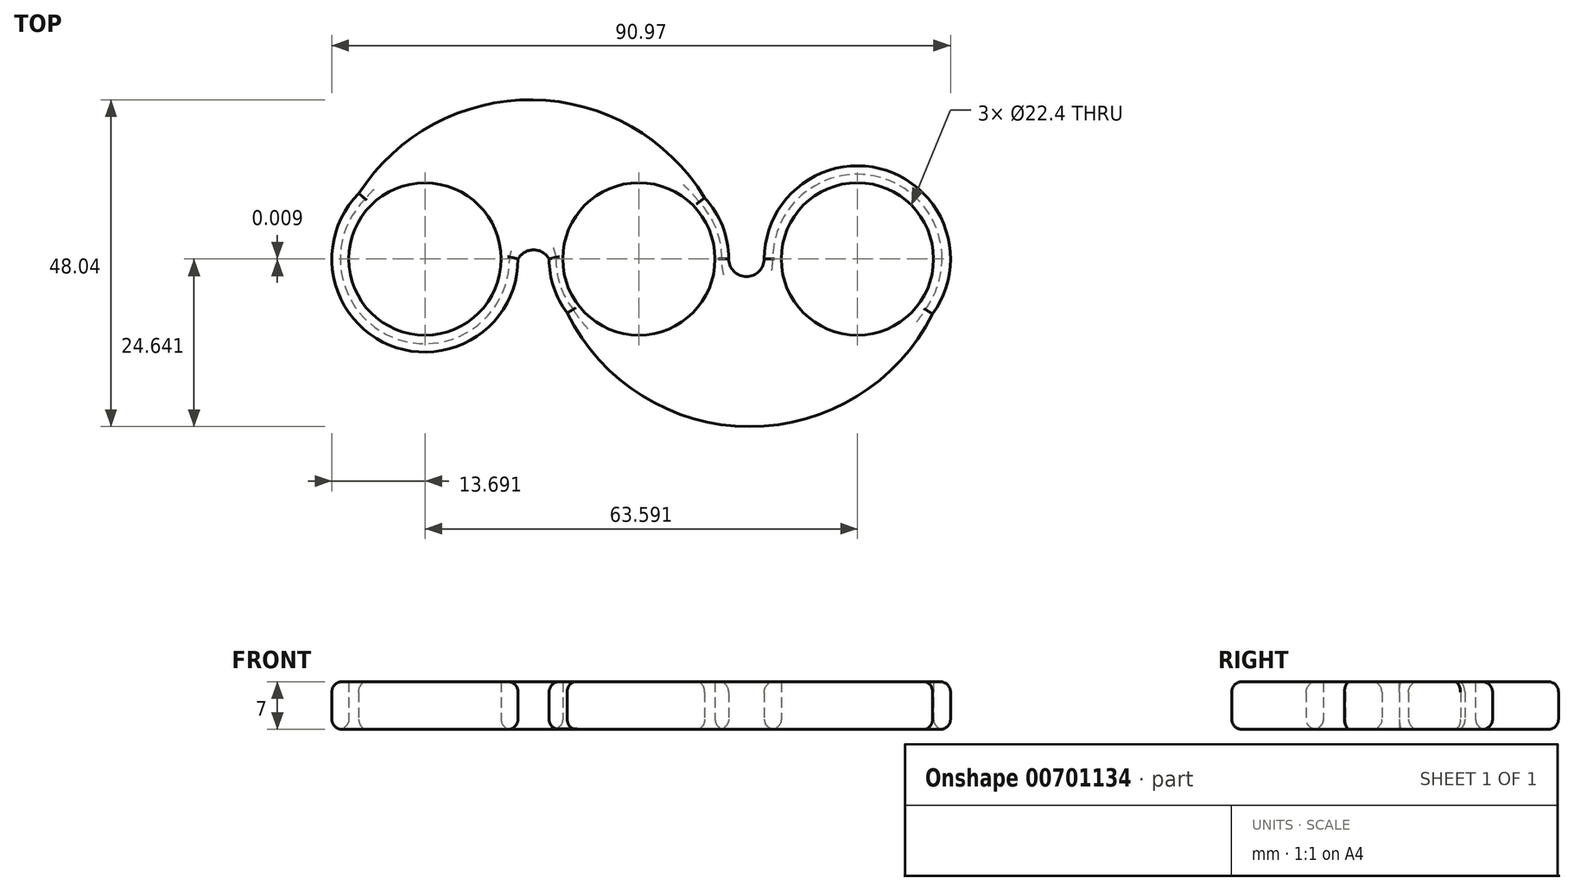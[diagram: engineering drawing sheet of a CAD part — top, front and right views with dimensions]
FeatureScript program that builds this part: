
annotation { "Feature Type Name" : "Feature", "Feature Type Description" : "" }
export const myFeature = defineFeature(function(context is Context, id is Id, definition is map)
    precondition{}
    {
        {
            var Q0;
            Q0=qCreatedBy(makeId("Top.planeOp"),FACE);
            var sketch = newSketch(context, id + "F0", { "sketchPlane" : qUnion([Q0])});
            skCircle(sketch, "E0", {"center": v(0, 0) * mm, "radius": 11.2 * mm});
            skArc(sketch, "E1", {"start": v(-13.2, 0) * mm, "mid": v(-10.57, -7.9) * mm, "end": v(-3.73, -12.66) * mm});
            skCircle(sketch, "E2", {"center": v(32.13, 0) * mm, "radius": 11.2 * mm});
            skArc(sketch, "E3", {"start": v(34.87, -13.41) * mm, "mid": v(40.79, 10.6) * mm, "end": v(18.44, 0) * mm});
            skArc(sketch, "E4.1.0", {"start": v(-33.9, 13.46) * mm, "mid": v(-40.23, -10.52) * mm, "end": v(-17.77, 0) * mm});
            skCircle(sketch, "E4.1.1", {"center": v(-31.46, 0) * mm, "radius": 11.2 * mm});
            skPoint(sketch, "E4.center", {"position": v(0.34, 0) * mm});
            skArc(sketch, "E5", {"start": v(-13.2, 0) * mm, "mid": v(-15.48, 1.34) * mm, "end": v(-17.77, 0) * mm});
            skArc(sketch, "E6", {"start": v(13.2, 0) * mm, "mid": v(15.82, -2.58) * mm, "end": v(18.44, 0) * mm});
            skArc(sketch, "E7", {"start": v(9.68, 8.98) * mm, "mid": v(-15.58, 23.4) * mm, "end": v(-41.2, 9.62) * mm});
            skArc(sketch, "E8", {"start": v(-10.54, -7.95) * mm, "mid": v(16.28, -24.65) * mm, "end": v(43.18, -8.08) * mm});
            skArc(sketch, "E9", {"start": v(0.9, 13.17) * mm, "mid": v(-16.44, 20.37) * mm, "end": v(-33.9, 13.46) * mm});
            skArc(sketch, "E10", {"start": v(-3.73, -12.66) * mm, "mid": v(15.4, -22.15) * mm, "end": v(34.87, -13.41) * mm});
            skArc(sketch, "E11.trimOffspring", {"start": v(13.2, 0) * mm, "mid": v(9.65, 9) * mm, "end": v(0.9, 13.17) * mm});
            skSolve(sketch);
        }
        {
            var Q0;
            Q0=makeQuery(id+"F0.imprint","IMPRINT",FACE,{"disambiguationData":[TD([[makeQuery(id+"F0.imprint","IMPRINT",EDGE,{"derivedFrom":sQuery(id+"F0.wireOp",EDGE,"E0")}),-1.0]])]});
            var Q1;
            {var subQ2=sQuery(id+"F0.wireOp",EDGE,"E7");Q1=makeQuery(id+"F0.imprint","IMPRINT",FACE,{"disambiguationData":[TD([[makeQuery(id+"F0.imprint","IMPRINT",EDGE,{"derivedFrom":subQ2}),1.0]])]});}
            var Q2;
            {var subQ2=sQuery(id+"F0.wireOp",EDGE,"E8");Q2=makeQuery(id+"F0.imprint","IMPRINT",FACE,{"disambiguationData":[TD([[makeQuery(id+"F0.imprint","IMPRINT",EDGE,{"derivedFrom":subQ2}),1.0]])]});}
            extrude(context, id + "F1", {"entities" : qUnion([Q0, Q1, Q2]), "depth" : 7 * mm, "offsetDistance" : 25 * mm});
        }
        {
            var Q0;
            Q0=makeQuery(id+"F1.opExtrude","CAP_EDGE",EDGE,{"disambiguationData":[OSD([sQuery(id+"F0.wireOp",EDGE,"E7")])],"isStart":false});
            var Q1;
            Q1=makeQuery(id+"F1.opExtrude","CAP_EDGE",EDGE,{"disambiguationData":[OSD([sQuery(id+"F0.wireOp",EDGE,"E4.1.0")])],"isStart":false});
            var Q2;
            Q2=makeQuery(id+"F1.opExtrude","CAP_EDGE",EDGE,{"disambiguationData":[OSD([sQuery(id+"F0.wireOp",EDGE,"E5")])],"isStart":false});
            var Q3;
            Q3=makeQuery(id+"F1.opExtrude","CAP_EDGE",EDGE,{"disambiguationData":[OSD([sQuery(id+"F0.wireOp",EDGE,"E1")])],"isStart":false});
            var Q4;
            Q4=makeQuery(id+"F1.opExtrude","CAP_EDGE",EDGE,{"disambiguationData":[OSD([sQuery(id+"F0.wireOp",EDGE,"E11.trimOffspring")])],"isStart":false});
            var Q5;
            Q5=makeQuery(id+"F1.opExtrude","CAP_EDGE",EDGE,{"disambiguationData":[OSD([sQuery(id+"F0.wireOp",EDGE,"E6")])],"isStart":false});
            var Q6;
            Q6=makeQuery(id+"F1.opExtrude","CAP_EDGE",EDGE,{"disambiguationData":[OSD([sQuery(id+"F0.wireOp",EDGE,"E3")])],"isStart":false});
            var Q7;
            Q7=makeQuery(id+"F1.opExtrude","CAP_EDGE",EDGE,{"disambiguationData":[OSD([sQuery(id+"F0.wireOp",EDGE,"E8")])],"isStart":false});
            var Q8;
            Q8=makeQuery(id+"F1.opExtrude","CAP_FACE",FACE,{"disambiguationData":[OSD([sQuery(id+"F0.wireOp",EDGE,"E0"),sQuery(id+"F0.wireOp",EDGE,"E1"),sQuery(id+"F0.wireOp",EDGE,"E2"),sQuery(id+"F0.wireOp",EDGE,"E3"),sQuery(id+"F0.wireOp",EDGE,"E4.1.0"),sQuery(id+"F0.wireOp",EDGE,"E4.1.1"),sQuery(id+"F0.wireOp",EDGE,"E5"),sQuery(id+"F0.wireOp",EDGE,"E6"),sQuery(id+"F0.wireOp",EDGE,"E7"),sQuery(id+"F0.wireOp",EDGE,"E8"),sQuery(id+"F0.wireOp",EDGE,"E11.trimOffspring")])],"isStart":true});
            fillet(context, id + "F2", {"entities" : qUnion([Q0, Q1, Q2, Q3, Q4, Q5, Q6, Q7, Q8]), "radius" : 1.5 * mm, "tangentPropagation" : true, "allowEdgeOverflow" : false});
        }
    });
